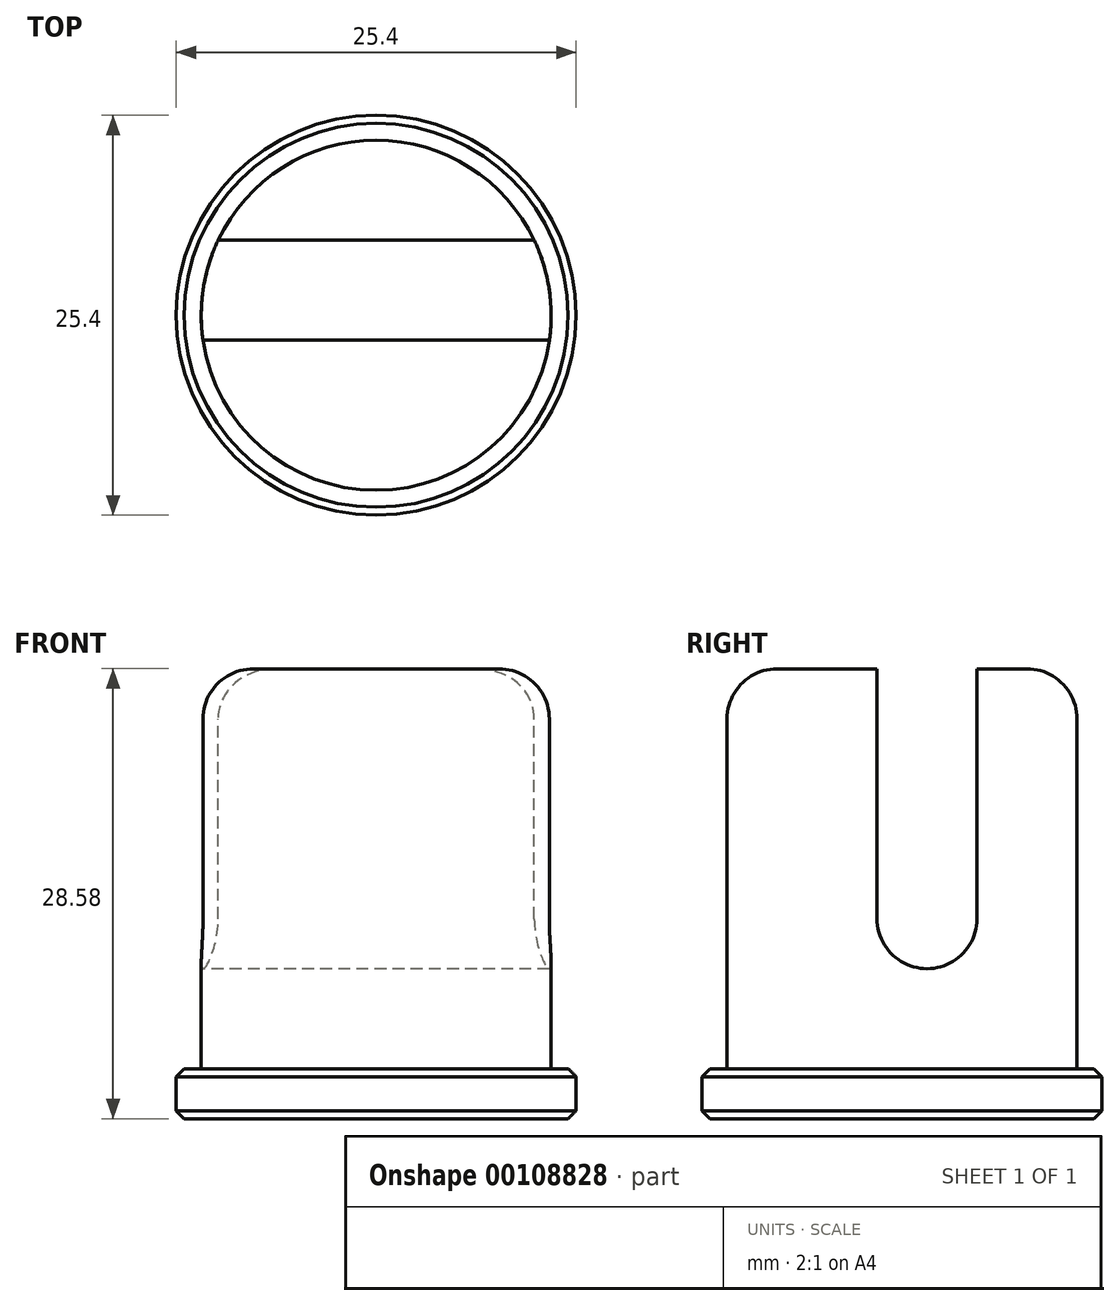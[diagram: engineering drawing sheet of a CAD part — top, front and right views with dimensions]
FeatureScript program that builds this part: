
annotation { "Feature Type Name" : "Feature", "Feature Type Description" : "" }
export const myFeature = defineFeature(function(context is Context, id is Id, definition is map)
    precondition{}
    {
        {
            var Q0;
            Q0=qCreatedBy(makeId("Top.planeOp"),FACE);
            var sketch = newSketch(context, id + "F0", { "sketchPlane" : qUnion([Q0])});
            skCircle(sketch, "E0", {"center": v(0, 0) * mm, "radius": 12.7 * mm});
            skSolve(sketch);
        }
        {
            var Q0;
            Q0=makeQuery(id+"F0.imprint","IMPRINT",FACE,{"disambiguationData":[TD([[makeQuery(id+"F0.imprint","IMPRINT",EDGE,{"derivedFrom":sQuery(id+"F0.wireOp",EDGE,"E0")}),1.0]])]});
            extrude(context, id + "F6", {"entities" : qUnion([Q0]), "depth" : 3.17 * mm});
        }
        {
            var Q0;
            Q0=makeQuery(id+"F6.opExtrude","CAP_FACE",FACE,{"disambiguationData":[OSD([sQuery(id+"F0.wireOp",EDGE,"E0")])],"isStart":false});
            var sketch = newSketch(context, id + "F7", { "sketchPlane" : qUnion([Q0])});
            skCircle(sketch, "E1", {"center": v(0, 0) * mm, "radius": 11.11 * mm});
            skSolve(sketch);
        }
        {
            var Q0;
            Q0=makeQuery(id+"F7.imprint","IMPRINT",FACE,{"disambiguationData":[TD([[makeQuery(id+"F7.imprint","IMPRINT",EDGE,{"derivedFrom":sQuery(id+"F7.wireOp",EDGE,"E1")}),1.0]])]});
            extrude(context, id + "F1", {"entities" : qUnion([Q0]), "operationType" : NewBodyOperationType.ADD, "depth" : 25.4 * mm});
        }
        {
            var Q0;
            Q0=makeQuery(id+"F1.opExtrude","CAP_FACE",FACE,{"disambiguationData":[OSD([sQuery(id+"F7.wireOp",EDGE,"E1")])],"isStart":false});
            var sketch = newSketch(context, id + "F2", { "sketchPlane" : qUnion([Q0])});
            skLineSegment(sketch, "E2", {"start": v(-10.04, 4.76) * mm, "end": v(10.04, 4.76) * mm});
            skLineSegment(sketch, "E3", {"start": v(-11, -1.59) * mm, "end": v(11, -1.59) * mm});
            skArc(sketch, "E4", {"start": v(10.04, 4.76) * mm, "mid": v(10.99, 1.66) * mm, "end": v(11, -1.59) * mm});
            skArc(sketch, "E5", {"start": v(-10.04, 4.76) * mm, "mid": v(-10.99, 1.66) * mm, "end": v(-11, -1.59) * mm});
            skSolve(sketch);
        }
        {
            var Q0;
            Q0 = qSketchRegion(id + "F2", true);
            var sketch = newSketch(context, id + "F8", { "sketchPlane" : qUnion([Q0])});
            skSolve(sketch);
        }
        {
            var Q0;
            Q0 = qSketchRegion(id + "F8", true);
            var Q1;
            Q1=makeQuery(id+"F2.imprint","IMPRINT",FACE,{"disambiguationData":[TD([[makeQuery(id+"F2.imprint","IMPRINT",EDGE,{"derivedFrom":sQuery(id+"F2.wireOp",EDGE,"E2")}),-1.0]])]});
            extrude(context, id + "F9", {"entities" : qUnion([Q0, Q1]), "operationType" : NewBodyOperationType.REMOVE, "oppositeDirection" : true, "depth" : 19.05 * mm});
        }
        {
            var Q0;
            Q0=makeQuery(id+"F9.boolean.opBoolean","COPY",EDGE,{"derivedFrom":makeQuery(id+"F9.opExtrude","CAP_EDGE",EDGE,{"disambiguationData":[OSD([sQuery(id+"F2.wireOp",EDGE,"E2")])],"isStart":false})});
            var Q1;
            Q1=makeQuery(id+"F9.boolean.opBoolean","COPY",EDGE,{"derivedFrom":makeQuery(id+"F9.opExtrude","CAP_EDGE",EDGE,{"disambiguationData":[OSD([sQuery(id+"F2.wireOp",EDGE,"E3")])],"isStart":false})});
            fillet(context, id + "F3", {"entities" : qUnion([Q0, Q1]), "radius" : 3.17 * mm, "tangentPropagation" : true, "allowEdgeOverflow" : false});
        }
        {
            var Q0;
            {var subQ0=sQuery(id+"F7.wireOp",EDGE,"E1");Q0=makeQuery(id+"F9.boolean.opBoolean","SPLIT",EDGE,{"disambiguationData":[TD([makeQuery(id+"F9.opExtrude","SWEPT_FACE",FACE,{"disambiguationData":[OSD([sQuery(id+"F2.wireOp",EDGE,"E2")])]})])],"derivedFrom":makeQuery(id+"F1.opExtrude","CAP_EDGE",EDGE,{"disambiguationData":[OSD([subQ0])],"isStart":false})});}
            var Q1;
            {var subQ0=sQuery(id+"F7.wireOp",EDGE,"E1");Q1=makeQuery(id+"F9.boolean.opBoolean","SPLIT",EDGE,{"disambiguationData":[TD([makeQuery(id+"F9.opExtrude","SWEPT_FACE",FACE,{"disambiguationData":[OSD([sQuery(id+"F2.wireOp",EDGE,"E3")])]})])],"derivedFrom":makeQuery(id+"F1.opExtrude","CAP_EDGE",EDGE,{"disambiguationData":[OSD([subQ0])],"isStart":false})});}
            fillet(context, id + "F4", {"entities" : qUnion([Q0, Q1]), "radius" : 3.17 * mm, "tangentPropagation" : true, "allowEdgeOverflow" : false});
        }
        {
            var Q0;
            Q0=makeQuery(id+"F6.opExtrude","CAP_EDGE",EDGE,{"disambiguationData":[OSD([sQuery(id+"F0.wireOp",EDGE,"E0")])],"isStart":false});
            var Q1;
            Q1=makeQuery(id+"F6.opExtrude","CAP_EDGE",EDGE,{"disambiguationData":[OSD([sQuery(id+"F0.wireOp",EDGE,"E0")])],"isStart":true});
            chamfer(context, id + "F5", {"entities" : qUnion([Q0, Q1]), "width" : 0.5 * mm, "tangentPropagation" : true});
        }
    });
